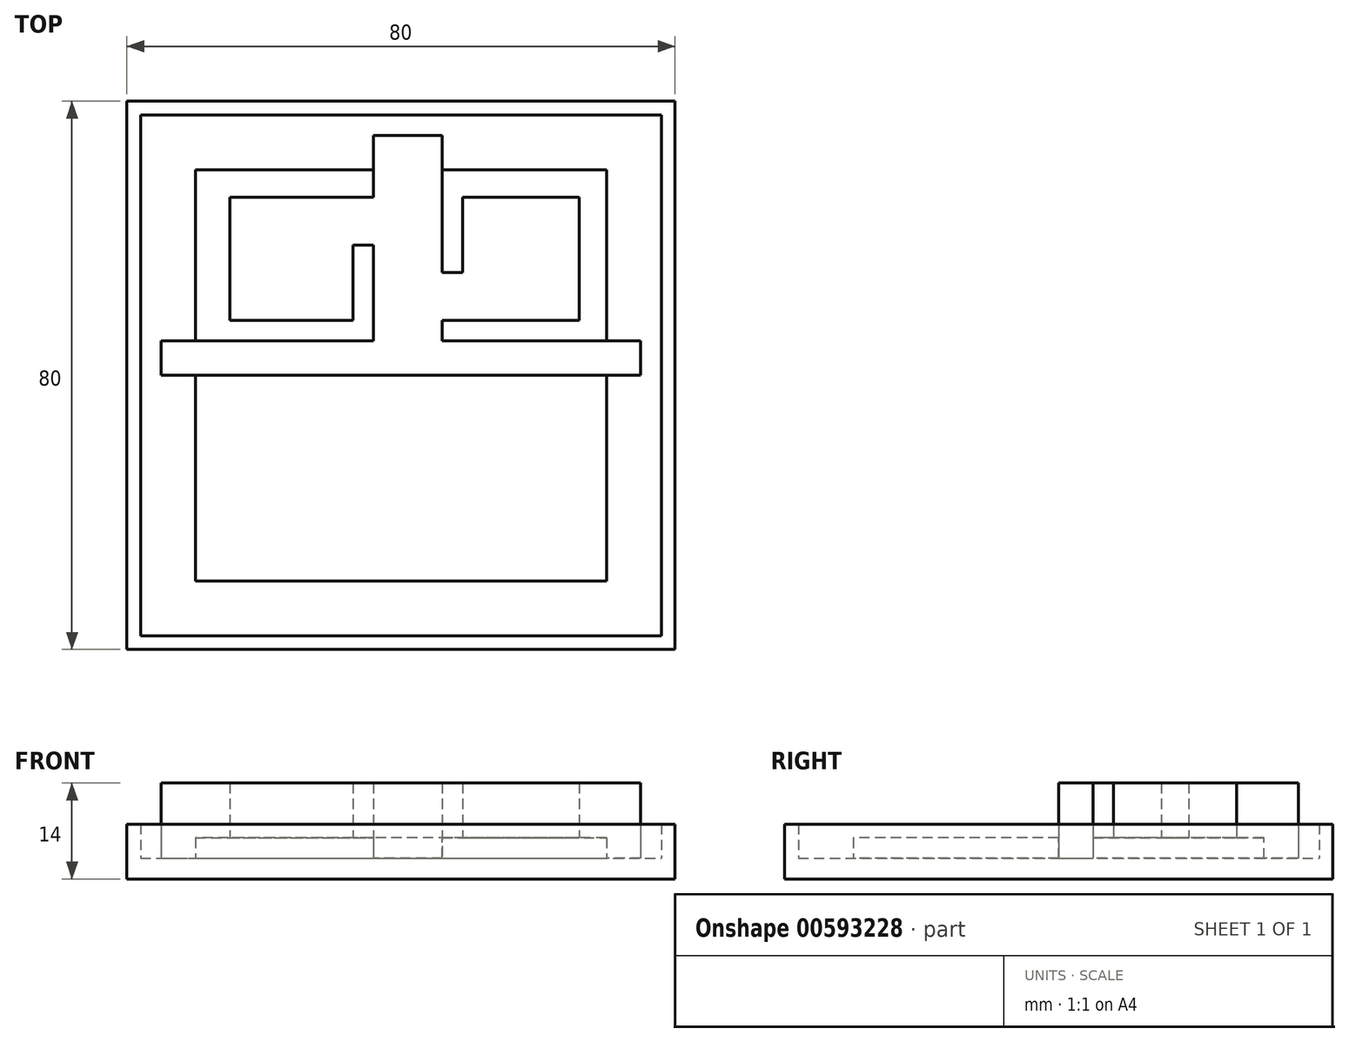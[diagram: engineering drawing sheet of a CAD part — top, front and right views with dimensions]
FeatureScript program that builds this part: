
annotation { "Feature Type Name" : "Feature", "Feature Type Description" : "" }
export const myFeature = defineFeature(function(context is Context, id is Id, definition is map)
    precondition{}
    {
        {
            var Q0;
            Q0=qCreatedBy(makeId("Top.planeOp"),FACE);
            var sketch = newSketch(context, id + "F0", { "sketchPlane" : qUnion([Q0])});
            skLineSegment(sketch, "E0.bottom", {"start": v(-35, 35) * mm, "end": v(35, 35) * mm});
            skLineSegment(sketch, "E0.top", {"start": v(-35, -35) * mm, "end": v(35, -35) * mm});
            skLineSegment(sketch, "E0.left", {"start": v(-35, 35) * mm, "end": v(-35, -35) * mm});
            skLineSegment(sketch, "E0.right", {"start": v(35, 35) * mm, "end": v(35, -35) * mm});
            skLineSegment(sketch, "E1.bottom", {"start": v(-40, 40) * mm, "end": v(40, 40) * mm});
            skLineSegment(sketch, "E1.top", {"start": v(-40, -40) * mm, "end": v(40, -40) * mm});
            skLineSegment(sketch, "E1.left", {"start": v(-40, 40) * mm, "end": v(-40, -40) * mm});
            skLineSegment(sketch, "E1.right", {"start": v(40, 40) * mm, "end": v(40, -40) * mm});
            skLineSegment(sketch, "E2.bottom", {"start": v(-38, -38) * mm, "end": v(38, -38) * mm});
            skLineSegment(sketch, "E2.top", {"start": v(-38, 38) * mm, "end": v(38, 38) * mm});
            skLineSegment(sketch, "E2.left", {"start": v(-38, -38) * mm, "end": v(-38, 38) * mm});
            skLineSegment(sketch, "E2.right", {"start": v(38, -38) * mm, "end": v(38, 38) * mm});
            skSolve(sketch);
        }
        {
            var Q0;
            Q0 = qSketchRegion(id + "F0", true);
            extrude(context, id + "F1", {"entities" : qUnion([Q0]), "depth" : 54 * mm, "offsetDistance" : 25 * mm, "hasSecondDirection" : true, "secondDirectionOppositeDirection" : true, "secondDirectionDepth" : -3 * mm});
        }
        {
            var Q0;
            Q0 = qSketchRegion(id + "F0", true);
            var Q1;
            Q1=makeQuery(id+"F0.imprint","IMPRINT",FACE,{"disambiguationData":[TD([[makeQuery(id+"F0.imprint","IMPRINT",EDGE,{"derivedFrom":sQuery(id+"F0.wireOp",EDGE,"E0.bottom")}),-1.0]])]});
            var Q2;
            Q2=makeQuery(id+"F0.imprint","IMPRINT",FACE,{"disambiguationData":[TD([[makeQuery(id+"F0.imprint","IMPRINT",EDGE,{"derivedFrom":sQuery(id+"F0.wireOp",EDGE,"E0.bottom")}),1.0]])]});
            extrude(context, id + "F2", {"entities" : qUnion([Q0, Q1, Q2]), "operationType" : NewBodyOperationType.ADD, "oppositeDirection" : true, "depth" : 3 * mm, "offsetDistance" : 25 * mm});
        }
        {
            var Q0;
            Q0=qCreatedBy(makeId("Top.planeOp"),FACE);
            var sketch = newSketch(context, id + "F3", { "sketchPlane" : qUnion([Q0])});
            skLineSegment(sketch, "E3.bottom", {"start": v(-25, 16) * mm, "end": v(20, 16) * mm});
            skLineSegment(sketch, "E3.top", {"start": v(-25, 8) * mm, "end": v(20, 8) * mm});
            skLineSegment(sketch, "E3.left", {"start": v(-25, 16) * mm, "end": v(-25, 8) * mm});
            skLineSegment(sketch, "E3.right", {"start": v(25, 27) * mm, "end": v(25, -25) * mm});
            skLineSegment(sketch, "E4.bottom", {"start": v(20, 5) * mm, "end": v(-25, 5) * mm});
            skLineSegment(sketch, "E4.top", {"start": v(20, -3) * mm, "end": v(-25, -3) * mm});
            skLineSegment(sketch, "E4.right", {"start": v(-25, 5) * mm, "end": v(-25, -3) * mm});
            skLineSegment(sketch, "E5.bottom", {"start": v(-25, -6) * mm, "end": v(20, -6) * mm});
            skLineSegment(sketch, "E5.top", {"start": v(-25, -14) * mm, "end": v(20, -14) * mm});
            skLineSegment(sketch, "E5.left", {"start": v(-25, -6) * mm, "end": v(-25, -14) * mm});
            skLineSegment(sketch, "E6.bottom", {"start": v(-25, -17) * mm, "end": v(20, -17) * mm});
            skLineSegment(sketch, "E6.top", {"start": v(-25, -25) * mm, "end": v(25, -25) * mm});
            skLineSegment(sketch, "E6.left", {"start": v(-25, -17) * mm, "end": v(-25, -25) * mm});
            skLineSegment(sketch, "E7.left", {"start": v(20, 8) * mm, "end": v(20, 5) * mm});
            skLineSegment(sketch, "E8.left", {"start": v(20, -3) * mm, "end": v(20, -6) * mm});
            skLineSegment(sketch, "E9.left", {"start": v(20, -14) * mm, "end": v(20, -17) * mm});
            skLineSegment(sketch, "E10.bottom", {"start": v(-25, 27) * mm, "end": v(25, 27) * mm});
            skLineSegment(sketch, "E10.top", {"start": v(-25, 19) * mm, "end": v(20, 19) * mm});
            skLineSegment(sketch, "E10.left", {"start": v(-25, 27) * mm, "end": v(-25, 19) * mm});
            skLineSegment(sketch, "E11", {"start": v(20, 16) * mm, "end": v(20, 19) * mm});
            skSolve(sketch);
        }
        {
            var Q0;
            Q0=qCreatedBy(makeId("Top.planeOp"),FACE);
            var sketch = newSketch(context, id + "F4", { "sketchPlane" : qUnion([Q0])});
            skLineSegment(sketch, "E12.bottom", {"start": v(-30, 30) * mm, "end": v(30, 30) * mm});
            skLineSegment(sketch, "E12.top", {"start": v(-30, -30) * mm, "end": v(30, -30) * mm});
            skLineSegment(sketch, "E12.left", {"start": v(-30, 30) * mm, "end": v(-30, -30) * mm});
            skLineSegment(sketch, "E12.right", {"start": v(30, 30) * mm, "end": v(30, -30) * mm});
            skSolve(sketch);
        }
        {
            var Q0;
            Q0 = qSketchRegion(id + "F4", true);
            extrude(context, id + "F5", {"entities" : qUnion([Q0]), "operationType" : NewBodyOperationType.ADD, "depth" : 3 * mm, "offsetDistance" : 25 * mm});
        }
        {
            var Q0;
            Q0=makeQuery(id+"F1.opExtrude","SWEPT_BODY",BODY,{"disambiguationData":[OSD([sQuery(id+"F0.wireOp",EDGE,"E0.bottom"),sQuery(id+"F0.wireOp",EDGE,"E0.top"),sQuery(id+"F0.wireOp",EDGE,"E0.left"),sQuery(id+"F0.wireOp",EDGE,"E0.right"),sQuery(id+"F0.wireOp",EDGE,"E1.bottom"),sQuery(id+"F0.wireOp",EDGE,"E1.top"),sQuery(id+"F0.wireOp",EDGE,"E1.left"),sQuery(id+"F0.wireOp",EDGE,"E1.right")])]});
            deleteBodies(context, id + "F6", {"entities" : qUnion([Q0])});
        }
        {
            var Q0;
            Q0=makeQuery(id+"F0.imprint","IMPRINT",FACE,{"disambiguationData":[TD([[makeQuery(id+"F0.imprint","IMPRINT",EDGE,{"derivedFrom":sQuery(id+"F0.wireOp",EDGE,"E1.bottom")}),-1.0]])]});
            extrude(context, id + "F7", {"entities" : qUnion([Q0]), "operationType" : NewBodyOperationType.ADD, "depth" : 5 * mm, "offsetDistance" : 25 * mm});
        }
        {
            var Q0;
            Q0=qCreatedBy(makeId("Top.planeOp"),FACE);
            var sketch = newSketch(context, id + "F8", { "sketchPlane" : qUnion([Q0])});
            skLineSegment(sketch, "E13", {"start": v(35, 0) * mm, "end": v(35, 5) * mm});
            skLineSegment(sketch, "E14", {"start": v(35, 5) * mm, "end": v(6, 5) * mm});
            skLineSegment(sketch, "E15", {"start": v(6, 5) * mm, "end": v(6, 8) * mm});
            skLineSegment(sketch, "E16", {"start": v(6, 8) * mm, "end": v(26, 8) * mm});
            skLineSegment(sketch, "E17", {"start": v(26, 8) * mm, "end": v(26, 26) * mm});
            skLineSegment(sketch, "E18", {"start": v(26, 26) * mm, "end": v(9, 26) * mm});
            skLineSegment(sketch, "E19", {"start": v(6, 35) * mm, "end": v(-4, 35) * mm});
            skLineSegment(sketch, "E20", {"start": v(-4, 35) * mm, "end": v(-4, 26) * mm});
            skLineSegment(sketch, "E21", {"start": v(-4, 26) * mm, "end": v(-25, 26) * mm});
            skLineSegment(sketch, "E22", {"start": v(-25, 26) * mm, "end": v(-25, 8) * mm});
            skLineSegment(sketch, "E23", {"start": v(-25, 8) * mm, "end": v(-7, 8) * mm});
            skLineSegment(sketch, "E24", {"start": v(-4, 19) * mm, "end": v(-4, 5) * mm});
            skLineSegment(sketch, "E25", {"start": v(-35, 5) * mm, "end": v(-35, 0) * mm});
            skLineSegment(sketch, "E26", {"start": v(-35, 0) * mm, "end": v(35, 0) * mm});
            skLineSegment(sketch, "E27", {"start": v(-35, 5) * mm, "end": v(-4, 5) * mm});
            skLineSegment(sketch, "E28", {"start": v(-7, 8) * mm, "end": v(-7, 19) * mm});
            skLineSegment(sketch, "E29", {"start": v(-7, 19) * mm, "end": v(-4, 19) * mm});
            skLineSegment(sketch, "E30", {"start": v(6, 15) * mm, "end": v(6, 35) * mm});
            skLineSegment(sketch, "E31", {"start": v(9, 26) * mm, "end": v(9, 15) * mm});
            skLineSegment(sketch, "E32", {"start": v(9, 15) * mm, "end": v(6, 15) * mm});
            skSolve(sketch);
        }
        {
            var Q0;
            Q0 = qSketchRegion(id + "F8", true);
            extrude(context, id + "F9", {"entities" : qUnion([Q0]), "operationType" : NewBodyOperationType.ADD, "depth" : 11 * mm, "offsetDistance" : 25 * mm});
        }
    });
